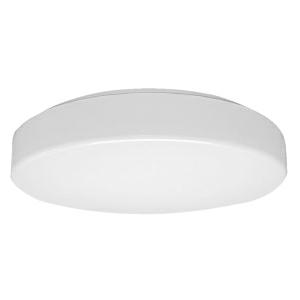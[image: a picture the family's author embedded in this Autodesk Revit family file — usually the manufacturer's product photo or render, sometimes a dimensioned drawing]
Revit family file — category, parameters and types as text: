
# Revit family: oblo_fit_-_oba_2000_830_00813348_7b03
name_source: partatom
category: Lighting Fixtures
units: mm (PartAtom-declared; Revit-internal decimal feet)

## family parameters
Cut with Voids When Loaded = No
Host = Face
Light Source = No
Part Type = Normal
Room Calculation Point = No
Round Connector Dimension = Use Diameter
Shared = No

## types (1)
- OBLO.fit - OBA 2000/830 (1 x LED, 2100 lm, 3000K)
    Apparent Load = 22 VA
    Approval mark = CE
    CIE Flux Codes = 41 72 91 84 100
    Color Rendering = 80-89
    Color Temperature = 3000K
    Control Gear = Electronic ballast
    Default Elevation = 1800 mm
    Description = OBA 2000/830|Surface-mounted luminaire.|light source:   Warm white   |work equipment: Power supply unit|luminous flux: 2100 lm|light distribution: Direct|class of protection: I|technology: Switchable|mains lead: Direct power supply|glare control: without|
    Frequency = 50 Hz, 60 Hz
    Height = 85 mm
    Lamp = 1 x LED
    Lamp Light Flux = 2100 lm
    Lamp count = 1
    Length = 370 mm
    Luminous efficacy = 95 lm/W
    Manufacturer = Waldmann
    ModVariant = No
    Model = 00813348
    Mounting Place = Ceiling
    Mounting Type = Surface mounted
    Number of Poles = 1
    OnlyDefault = Yes
    Power Factor = 1
    Product Name = OBLO.fit - OBA 2000/830
    Product group = Ceiling mounted luminaire
    ProductGroupID = 3
    Protection Class = Protection class I
    Protection Degree = IP 40
    RLX_Detail_Level = 1
    RLX_Emergency_Light_Flux = 0 lm
    RLX_Emergency_Type = 0
    RLX_Emergency_Type_DB = No
    RlxData = <blob elided: 22241 chars, md5=11c77a5f>
    Socket = socket
    Standby Power = 0 W
    System Light Flux = 2100 lm
    System Power = 22 W
    Type Comments = Product without accessories
    Type Image = oblo_led.jpg
    URL = http://relux.com
    VarID = ---
    Voltage = 230 V
    Voltage Range = 220-240 V
    Weight = 0.00 kg
    Width = 0 mm  [stored 0 ft]

note: [stored X ft] marks values corroborated as IEEE doubles in the binary element streams (Revit-internal decimal feet)

## geometry (parser evidence)
native form markers: Blend x4, Sweep x11
no freeform markers — native parametric forms only
